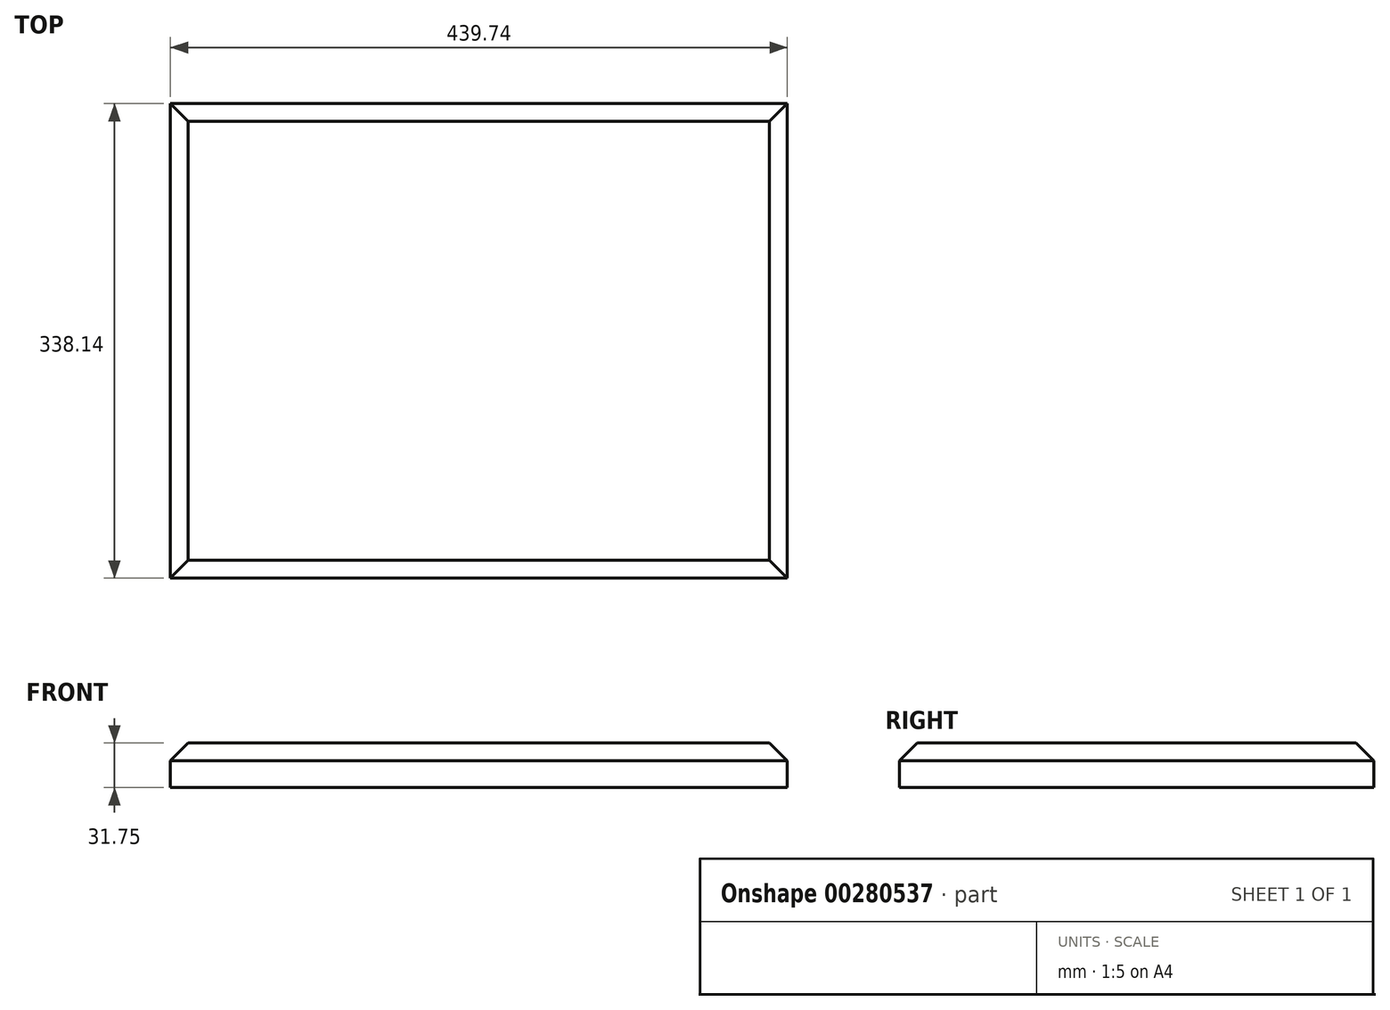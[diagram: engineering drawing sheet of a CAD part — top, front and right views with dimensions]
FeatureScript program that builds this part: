
annotation { "Feature Type Name" : "Feature", "Feature Type Description" : "" }
export const myFeature = defineFeature(function(context is Context, id is Id, definition is map)
    precondition{}
    {
        {
            var Q0;
            Q0=qCreatedBy(makeId("Top.planeOp"),FACE);
            var sketch = newSketch(context, id + "F0", { "sketchPlane" : qUnion([Q0])});
            skLineSegment(sketch, "E0.bottom", {"start": v(219.87, 169.07) * mm, "end": v(-219.87, 169.07) * mm});
            skLineSegment(sketch, "E0.top", {"start": v(219.87, -169.07) * mm, "end": v(-219.87, -169.07) * mm});
            skLineSegment(sketch, "E0.left", {"start": v(219.87, 169.07) * mm, "end": v(219.87, -169.07) * mm});
            skLineSegment(sketch, "E0.right", {"start": v(-219.87, 169.07) * mm, "end": v(-219.87, -169.07) * mm});
            skPoint(sketch, "E0.middle", {"position": v(0, 0) * mm});
            skSolve(sketch);
        }
        {
            var Q0;
            Q0=makeQuery(id+"F0.imprint","IMPRINT",FACE,{"disambiguationData":[TD([[makeQuery(id+"F0.imprint","IMPRINT",EDGE,{"derivedFrom":sQuery(id+"F0.wireOp",EDGE,"E0.bottom")}),1.0]])]});
            extrude(context, id + "F1", {"entities" : qUnion([Q0]), "depth" : 31.75 * mm});
        }
        {
            var Q0;
            Q0=makeQuery(id+"F1.opExtrude","CAP_EDGE",EDGE,{"disambiguationData":[OSD([sQuery(id+"F0.wireOp",EDGE,"E0.right")])],"isStart":false});
            var Q1;
            Q1=makeQuery(id+"F1.opExtrude","CAP_EDGE",EDGE,{"disambiguationData":[OSD([sQuery(id+"F0.wireOp",EDGE,"E0.top")])],"isStart":false});
            var Q2;
            Q2=makeQuery(id+"F1.opExtrude","CAP_EDGE",EDGE,{"disambiguationData":[OSD([sQuery(id+"F0.wireOp",EDGE,"E0.left")])],"isStart":false});
            var Q3;
            Q3=makeQuery(id+"F1.opExtrude","CAP_EDGE",EDGE,{"disambiguationData":[OSD([sQuery(id+"F0.wireOp",EDGE,"E0.bottom")])],"isStart":false});
            chamfer(context, id + "F2", {"entities" : qUnion([Q0, Q1, Q2, Q3]), "width" : 12.7 * mm, "tangentPropagation" : true});
        }
    });
